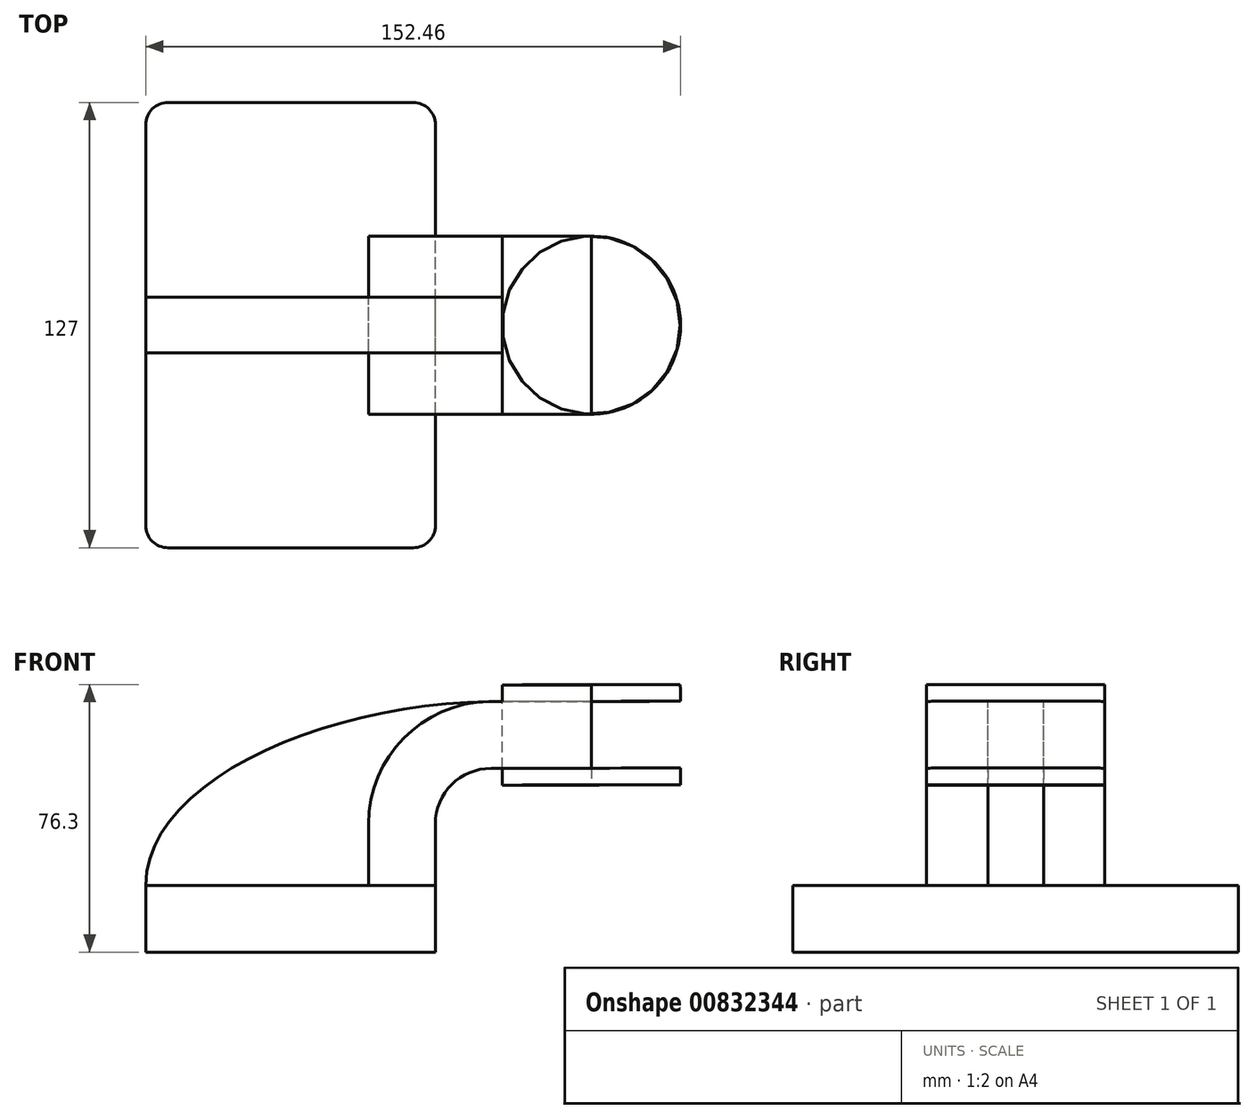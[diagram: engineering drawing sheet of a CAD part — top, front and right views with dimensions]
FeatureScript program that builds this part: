
annotation { "Feature Type Name" : "Feature", "Feature Type Description" : "" }
export const myFeature = defineFeature(function(context is Context, id is Id, definition is map)
    precondition{}
    {
        {
            var Q0;
            Q0=qCreatedBy(makeId("Front.planeOp"),FACE);
            var sketch = newSketch(context, id + "F0", { "sketchPlane" : qUnion([Q0])});
            skLineSegment(sketch, "E0.bottom", {"start": v(-41.28, -9.53) * mm, "end": v(41.28, -9.53) * mm});
            skLineSegment(sketch, "E0.top", {"start": v(-41.28, 9.52) * mm, "end": v(41.27, 9.52) * mm});
            skLineSegment(sketch, "E0.left", {"start": v(-41.27, -9.53) * mm, "end": v(-41.28, 9.52) * mm});
            skLineSegment(sketch, "E0.right", {"start": v(41.28, -9.53) * mm, "end": v(41.27, 9.52) * mm});
            skPoint(sketch, "E0.middle", {"position": v(0, 0) * mm});
            skLineSegment(sketch, "E1.bottom", {"start": v(111.12, 38.1) * mm, "end": v(60.32, 38.1) * mm});
            skLineSegment(sketch, "E1.top", {"start": v(111.12, 66.68) * mm, "end": v(60.32, 66.68) * mm});
            skLineSegment(sketch, "E1.left", {"start": v(111.12, 38.1) * mm, "end": v(111.12, 66.68) * mm});
            skLineSegment(sketch, "E1.right", {"start": v(60.32, 38.1) * mm, "end": v(60.32, 66.68) * mm});
            skPoint(sketch, "E1.middle", {"position": v(85.72, 52.39) * mm});
            skLineSegment(sketch, "E2", {"start": v(41.27, 9.52) * mm, "end": v(41.27, 27) * mm});
            skArc(sketch, "E3", {"start": v(41.27, 27) * mm, "mid": v(45.92, 38.23) * mm, "end": v(57.15, 42.88) * mm});
            skLineSegment(sketch, "E4", {"start": v(57.15, 42.88) * mm, "end": v(85.75, 42.88) * mm});
            skLineSegment(sketch, "E5.0", {"start": v(57.15, 61.93) * mm, "end": v(94.51, 61.93) * mm});
            skArc(sketch, "E5.1", {"start": v(22.22, 27) * mm, "mid": v(32.45, 51.7) * mm, "end": v(57.15, 61.93) * mm});
            skLineSegment(sketch, "E5.2", {"start": v(22.23, 9.52) * mm, "end": v(22.23, 27) * mm});
            skLineSegment(sketch, "E6", {"start": v(85.7, 66.68) * mm, "end": v(85.75, 38.1) * mm});
            skFitSpline(sketch, "E7", {"points": [v(-41.28, 9.53) * mm, v(57.15, 61.93) * mm], "startDerivative": vector(0, 90.29) * mm, "endDerivative": vector(138.8, 1) * mm});
            skLineSegment(sketch, "E8", {"start": v(94.51, 61.93) * mm, "end": v(111.12, 61.93) * mm});
            skLineSegment(sketch, "E9", {"start": v(85.75, 42.88) * mm, "end": v(111.12, 42.88) * mm});
            skLineSegment(sketch, "E10", {"start": v(111.12, 61.93) * mm, "end": v(111.12, 42.88) * mm});
            skLineSegment(sketch, "E11", {"start": v(60.32, 61.93) * mm, "end": v(111.12, 61.93) * mm});
            skLineSegment(sketch, "E12", {"start": v(60.32, 42.88) * mm, "end": v(111.12, 42.88) * mm});
            skLineSegment(sketch, "E13", {"start": v(60.32, 66.68) * mm, "end": v(60.32, 38.1) * mm});
            skLineSegment(sketch, "E14", {"start": v(111.12, 66.68) * mm, "end": v(111.12, 38.1) * mm});
            skSolve(sketch);
        }
        {
            var Q0;
            Q0=makeQuery(id+"F0.imprint","IMPRINT",FACE,{"disambiguationData":[TD([[makeQuery(id+"F0.imprint","IMPRINT",EDGE,{"derivedFrom":sQuery(id+"F0.wireOp",EDGE,"E0.bottom")}),1.0]])]});
            extrude(context, id + "F1", {"entities" : qUnion([Q0]), "endBound" : BoundingType.SYMMETRIC, "depth" : 127 * mm, "offsetDistance" : 25.4 * mm});
        }
        {
            var Q0;
            {var subQ1=sQuery(id+"F0.wireOp",EDGE,"E2");Q0=makeQuery(id+"F0.imprint","IMPRINT",FACE,{"disambiguationData":[TD([[makeQuery(id+"F0.imprint","IMPRINT",EDGE,{"derivedFrom":subQ1}),1.0]])]});}
            var Q1;
            {var subQ1=sQuery(id+"F0.wireOp",EDGE,"E11");var subQ3=sQuery(id+"F0.wireOp",EDGE,"E6");var subQ4=makeQuery(id+"F0.imprint","INTERSECT",VERTEX,{"derivedFrom":[subQ1,subQ3]});Q1=makeQuery(id+"F0.imprint","IMPRINT",FACE,{"disambiguationData":[TD([[makeQuery(id+"F0.imprint","IMPRINT",EDGE,{"disambiguationData":[TD([[subQ4,-1.0]])],"derivedFrom":subQ3}),-1.0]])]});}
            extrude(context, id + "F2", {"entities" : qUnion([Q0, Q1]), "endBound" : BoundingType.SYMMETRIC, "depth" : 50.8 * mm, "offsetDistance" : 25.4 * mm});
        }
        {
            var Q0;
            {var subQ3=sQuery(id+"F0.wireOp",EDGE,"E5.2");Q0=makeQuery(id+"F0.imprint","IMPRINT",FACE,{"disambiguationData":[TD([[makeQuery(id+"F0.imprint","IMPRINT",EDGE,{"derivedFrom":subQ3}),1.0]])]});}
            var Q1;
            {var subQ1=sQuery(id+"F0.wireOp",EDGE,"E2");Q1=makeQuery(id+"F0.imprint","IMPRINT",FACE,{"disambiguationData":[TD([[makeQuery(id+"F0.imprint","IMPRINT",EDGE,{"derivedFrom":subQ1}),1.0]])]});}
            extrude(context, id + "F3", {"entities" : qUnion([Q0, Q1]), "endBound" : BoundingType.SYMMETRIC, "depth" : 15.88 * mm, "offsetDistance" : 25.4 * mm});
        }
        {
            var Q0;
            {var subQ0=sQuery(id+"F0.wireOp",EDGE,"E14");var subQ1=sQuery(id+"F0.wireOp",EDGE,"E1.top");var subQ2=makeQuery(id+"F0.imprint","INTERSECT",VERTEX,{"derivedFrom":[subQ1,subQ0]});Q0=makeQuery(id+"F0.imprint","IMPRINT",FACE,{"disambiguationData":[TD([[makeQuery(id+"F0.imprint","IMPRINT",EDGE,{"disambiguationData":[TD([[subQ2,-1.0]])],"derivedFrom":subQ1}),1.0]])]});}
            var Q1;
            {var subQ0=sQuery(id+"F0.wireOp",EDGE,"E14");var subQ1=sQuery(id+"F0.wireOp",EDGE,"E11");var subQ2=makeQuery(id+"F0.imprint","INTERSECT",VERTEX,{"derivedFrom":[subQ1,subQ0]});Q1=makeQuery(id+"F0.imprint","IMPRINT",FACE,{"disambiguationData":[TD([[makeQuery(id+"F0.imprint","IMPRINT",EDGE,{"disambiguationData":[TD([[subQ2,1.0]])],"derivedFrom":subQ1}),-1.0]])]});}
            var Q2;
            {var subQ0=sQuery(id+"F0.wireOp",EDGE,"E14");var subQ1=sQuery(id+"F0.wireOp",EDGE,"E1.bottom");var subQ2=makeQuery(id+"F0.imprint","INTERSECT",VERTEX,{"derivedFrom":[subQ1,subQ0]});Q2=makeQuery(id+"F0.imprint","IMPRINT",FACE,{"disambiguationData":[TD([[makeQuery(id+"F0.imprint","IMPRINT",EDGE,{"disambiguationData":[TD([[subQ2,-1.0]])],"derivedFrom":subQ1}),-1.0]])]});}
            var Q3;
            Q3=sQuery(id+"F0.wireOp",EDGE,"E6");
            revolve(context, id + "F4", {"surfaceOperationType" : NewSurfaceOperationType.NEW, "entities" : qUnion([Q0, Q1, Q2]), "axis" : qUnion([Q3]), "revolveType" : RevolveType.FULL});
        }
        {
            var Q0;
            Q0=makeQuery(id+"F1.opExtrude","CAP_EDGE",EDGE,{"disambiguationData":[OSD([sQuery(id+"F0.wireOp",EDGE,"E0.right")])],"isStart":false});
            var Q1;
            Q1=makeQuery(id+"F1.opExtrude","CAP_EDGE",EDGE,{"disambiguationData":[OSD([sQuery(id+"F0.wireOp",EDGE,"E0.left")])],"isStart":false});
            var Q2;
            Q2=makeQuery(id+"F1.opExtrude","CAP_EDGE",EDGE,{"disambiguationData":[OSD([sQuery(id+"F0.wireOp",EDGE,"E0.right")])],"isStart":true});
            var Q3;
            Q3=makeQuery(id+"F1.opExtrude","CAP_EDGE",EDGE,{"disambiguationData":[OSD([sQuery(id+"F0.wireOp",EDGE,"E0.left")])],"isStart":true});
            fillet(context, id + "F5", {"entities" : qUnion([Q0, Q1, Q2, Q3]), "radius" : 6.35 * mm, "tangentPropagation" : true, "allowEdgeOverflow" : false});
        }
    });
